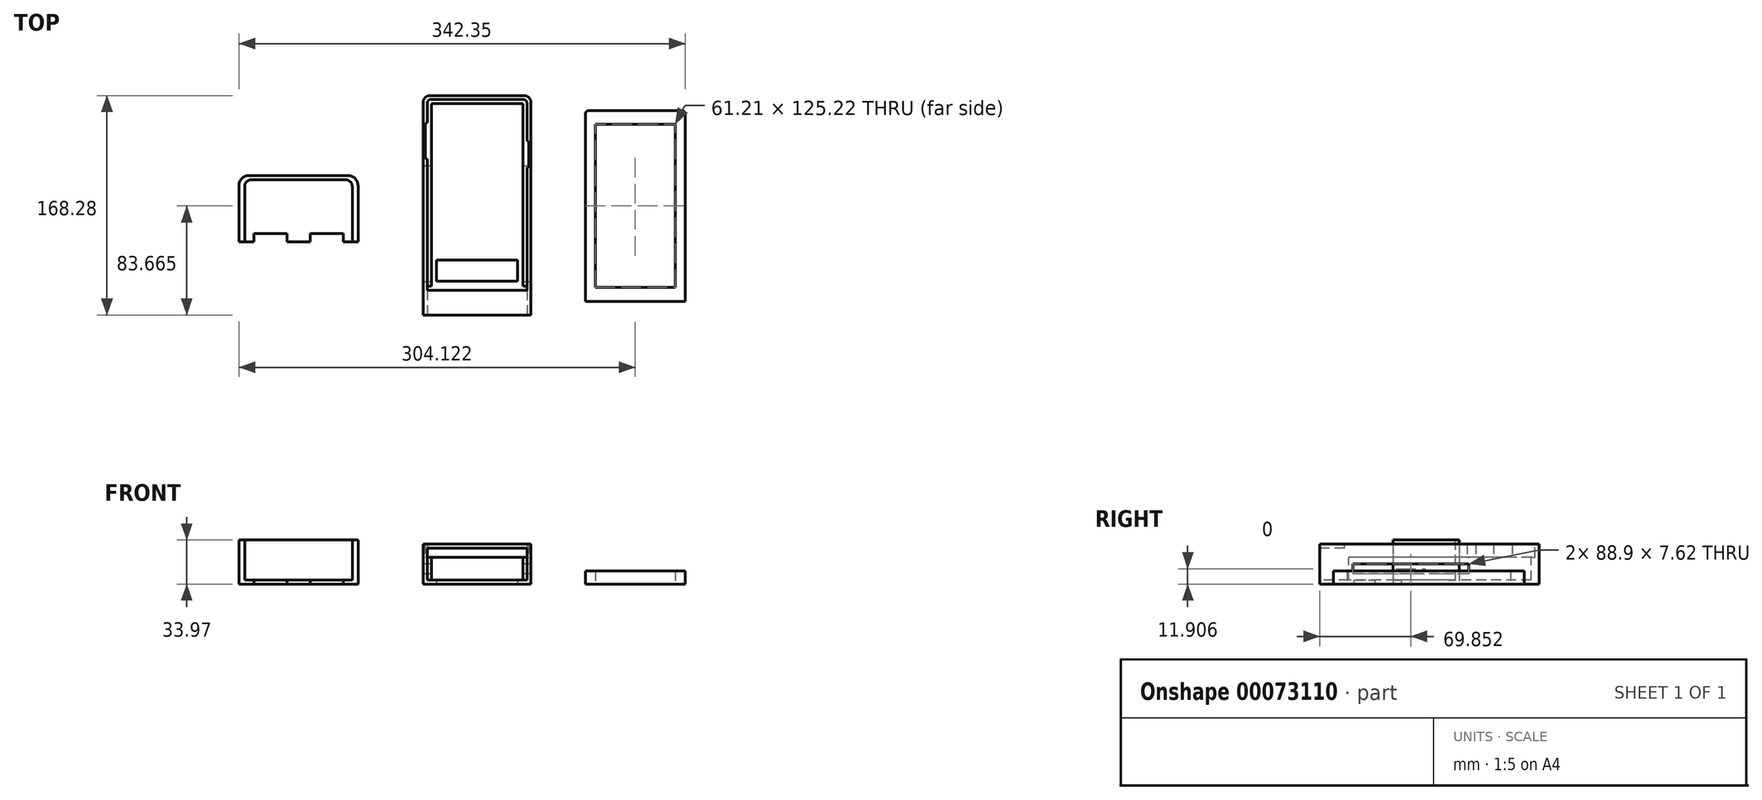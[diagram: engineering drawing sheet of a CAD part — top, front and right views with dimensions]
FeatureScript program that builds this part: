
annotation { "Feature Type Name" : "Feature", "Feature Type Description" : "" }
export const myFeature = defineFeature(function(context is Context, id is Id, definition is map)
    precondition{}
    {
        {
            var Q0;
            Q0=qCreatedBy(makeId("Top.planeOp"),FACE);
            var sketch = newSketch(context, id + "F0", { "sketchPlane" : qUnion([Q0])});
            skLineSegment(sketch, "E0.0", {"start": v(-45.8, 72.92) * mm, "end": v(36.75, 72.92) * mm});
            skLineSegment(sketch, "E0.1", {"start": v(-45.8, 72.92) * mm, "end": v(-45.8, -79.48) * mm});
            skLineSegment(sketch, "E0.2", {"start": v(-45.8, -79.48) * mm, "end": v(36.75, -79.48) * mm});
            skLineSegment(sketch, "E0.3", {"start": v(36.75, 72.92) * mm, "end": v(36.75, -79.48) * mm});
            skLineSegment(sketch, "E1", {"start": v(-45.8, -79.48) * mm, "end": v(-45.8, -95.36) * mm});
            skLineSegment(sketch, "E2", {"start": v(-45.8, -95.36) * mm, "end": v(36.75, -95.36) * mm});
            skLineSegment(sketch, "E3", {"start": v(36.75, -95.36) * mm, "end": v(36.75, -79.48) * mm});
            skLineSegment(sketch, "E4.bottom", {"start": v(-35.64, -69.32) * mm, "end": v(26.6, -69.32) * mm});
            skLineSegment(sketch, "E4.top", {"start": v(-35.64, -53.14) * mm, "end": v(26.6, -53.14) * mm});
            skLineSegment(sketch, "E4.left", {"start": v(-35.64, -69.32) * mm, "end": v(-35.64, -53.14) * mm});
            skLineSegment(sketch, "E4.right", {"start": v(26.6, -69.32) * mm, "end": v(26.6, -53.14) * mm});
            skSolve(sketch);
        }
        {
            var Q0;
            Q0=makeQuery(id+"F0.imprint","IMPRINT",FACE,{"disambiguationData":[TD([[makeQuery(id+"F0.imprint","IMPRINT",EDGE,{"derivedFrom":sQuery(id+"F0.wireOp",EDGE,"E0.0")}),-1.0]])]});
            extrude(context, id + "F1", {"entities" : qUnion([Q0]), "depth" : 30.8 * mm});
        }
        {
            var Q0;
            Q0=makeQuery(id+"F1.opExtrude","CAP_FACE",FACE,{"disambiguationData":[OSD([sQuery(id+"F0.wireOp",EDGE,"E0.0"),sQuery(id+"F0.wireOp",EDGE,"E0.1"),sQuery(id+"F0.wireOp",EDGE,"E0.2"),sQuery(id+"F0.wireOp",EDGE,"E0.3")])],"isStart":false});
            var sketch = newSketch(context, id + "F2", { "sketchPlane" : qUnion([Q0])});
            skLineSegment(sketch, "E5.0", {"start": v(-42.75, 69.87) * mm, "end": v(-42.75, -76.44) * mm});
            skLineSegment(sketch, "E5.1", {"start": v(-42.75, 69.87) * mm, "end": v(33.7, 69.87) * mm});
            skLineSegment(sketch, "E5.2", {"start": v(33.7, 69.87) * mm, "end": v(33.7, -76.44) * mm});
            skLineSegment(sketch, "E5.3", {"start": v(-42.75, -76.44) * mm, "end": v(33.7, -76.44) * mm});
            skSolve(sketch);
        }
        {
            var Q0;
            Q0=makeQuery(id+"F2.imprint","IMPRINT",FACE,{"disambiguationData":[TD([[makeQuery(id+"F2.imprint","IMPRINT",EDGE,{"derivedFrom":sQuery(id+"F2.wireOp",EDGE,"E5.0")}),1.0]])]});
            extrude(context, id + "F3", {"entities" : qUnion([Q0]), "operationType" : NewBodyOperationType.REMOVE, "oppositeDirection" : true, "depth" : 10.16 * mm});
        }
        {
            var Q0;
            Q0=makeQuery(id+"F3.boolean.opBoolean","COPY",FACE,{"derivedFrom":makeQuery(id+"F3.opExtrude","CAP_FACE",FACE,{"disambiguationData":[OSD([sQuery(id+"F2.wireOp",EDGE,"E5.0"),sQuery(id+"F2.wireOp",EDGE,"E5.1"),sQuery(id+"F2.wireOp",EDGE,"E5.2"),sQuery(id+"F2.wireOp",EDGE,"E5.3")])],"isStart":false})});
            var sketch = newSketch(context, id + "F4", { "sketchPlane" : qUnion([Q0])});
            skLineSegment(sketch, "E6.0", {"start": v(-39.57, 66.7) * mm, "end": v(30.53, 66.7) * mm});
            skLineSegment(sketch, "E6.1", {"start": v(-39.57, 66.7) * mm, "end": v(-39.57, -73.26) * mm});
            skLineSegment(sketch, "E6.2", {"start": v(-39.57, -73.26) * mm, "end": v(30.53, -73.26) * mm});
            skLineSegment(sketch, "E6.3", {"start": v(30.53, 66.7) * mm, "end": v(30.53, -73.26) * mm});
            skSolve(sketch);
        }
        {
            var Q0;
            Q0=makeQuery(id+"F4.imprint","IMPRINT",FACE,{"disambiguationData":[TD([[makeQuery(id+"F4.imprint","IMPRINT",EDGE,{"derivedFrom":sQuery(id+"F4.wireOp",EDGE,"E6.0")}),-1.0]])]});
            extrude(context, id + "F5", {"entities" : qUnion([Q0]), "operationType" : NewBodyOperationType.REMOVE, "oppositeDirection" : true, "depth" : 17.59 * mm});
        }
        {
            var Q0;
            Q0=makeQuery(id+"F0.imprint","IMPRINT",FACE,{"disambiguationData":[TD([[makeQuery(id+"F0.imprint","IMPRINT",EDGE,{"derivedFrom":sQuery(id+"F0.wireOp",EDGE,"E0.2")}),-1.0]])]});
            extrude(context, id + "F6", {"entities" : qUnion([Q0]), "operationType" : NewBodyOperationType.ADD, "depth" : 30.8 * mm});
        }
        {
            var Q0;
            Q0=makeQuery(id+"F6.opExtrude","SWEPT_FACE",FACE,{"disambiguationData":[OSD([sQuery(id+"F0.wireOp",EDGE,"E2")])]});
            var sketch = newSketch(context, id + "F7", { "sketchPlane" : qUnion([Q0])});
            skLineSegment(sketch, "E7.0", {"start": v(-42.75, 27.75) * mm, "end": v(33.7, 27.75) * mm});
            skLineSegment(sketch, "E7.1", {"start": v(-42.75, 27.75) * mm, "end": v(-42.75, 3.05) * mm});
            skLineSegment(sketch, "E7.2", {"start": v(-42.75, 3.05) * mm, "end": v(33.7, 3.05) * mm});
            skLineSegment(sketch, "E7.3", {"start": v(33.7, 27.75) * mm, "end": v(33.7, 3.05) * mm});
            skSolve(sketch);
        }
        {
            var Q0;
            Q0=makeQuery(id+"F7.imprint","IMPRINT",FACE,{"disambiguationData":[TD([[makeQuery(id+"F7.imprint","IMPRINT",EDGE,{"derivedFrom":sQuery(id+"F7.wireOp",EDGE,"E7.0")}),-1.0]])]});
            var Q1;
            Q1=makeQuery(id+"F5.boolean.opBoolean","COPY",FACE,{"derivedFrom":makeQuery(id+"F5.opExtrude","SWEPT_FACE",FACE,{"disambiguationData":[OSD([sQuery(id+"F4.wireOp",EDGE,"E6.2")])]})});
            extrude(context, id + "F8", {"entities" : qUnion([Q0]), "operationType" : NewBodyOperationType.REMOVE, "endBound" : BoundingType.UP_TO_SURFACE, "oppositeDirection" : true, "endBoundEntityFace" : qUnion([Q1]), "depth" : 20.48 * mm});
        }
        {
            var Q0;
            Q0=makeQuery(id+"F6.boolean.opBoolean","MERGE",FACE,{"derivedFrom":[makeQuery(id+"F1.opExtrude","SWEPT_FACE",FACE,{"disambiguationData":[OSD([sQuery(id+"F0.wireOp",EDGE,"E0.1")])]}),makeQuery(id+"F6.opExtrude","SWEPT_FACE",FACE,{"disambiguationData":[OSD([sQuery(id+"F0.wireOp",EDGE,"E1")])]})]});
            var sketch = newSketch(context, id + "F9", { "sketchPlane" : qUnion([Q0])});
            skLineSegment(sketch, "E8.bottom", {"start": v(-18.94, 15.72) * mm, "end": v(69.96, 15.72) * mm});
            skLineSegment(sketch, "E8.top", {"start": v(-18.94, 8.1) * mm, "end": v(69.96, 8.1) * mm});
            skLineSegment(sketch, "E8.left", {"start": v(-18.94, 15.72) * mm, "end": v(-18.94, 8.1) * mm});
            skLineSegment(sketch, "E8.right", {"start": v(69.96, 15.72) * mm, "end": v(69.96, 8.1) * mm});
            skSolve(sketch);
        }
        {
            var Q0;
            Q0=makeQuery(id+"F9.imprint","IMPRINT",FACE,{"disambiguationData":[TD([[makeQuery(id+"F9.imprint","IMPRINT",EDGE,{"derivedFrom":sQuery(id+"F9.wireOp",EDGE,"E8.bottom")}),-1.0]])]});
            var Q1;
            Q1=makeQuery(id+"F6.boolean.opBoolean","MERGE",FACE,{"derivedFrom":[makeQuery(id+"F1.opExtrude","SWEPT_FACE",FACE,{"disambiguationData":[OSD([sQuery(id+"F0.wireOp",EDGE,"E0.3")])]}),makeQuery(id+"F6.opExtrude","SWEPT_FACE",FACE,{"disambiguationData":[OSD([sQuery(id+"F0.wireOp",EDGE,"E3")])]})]});
            extrude(context, id + "F10", {"entities" : qUnion([Q0]), "operationType" : NewBodyOperationType.REMOVE, "endBound" : BoundingType.UP_TO_SURFACE, "oppositeDirection" : true, "endBoundEntityFace" : qUnion([Q1]), "depth" : 25.4 * mm});
        }
        {
            var Q0;
            Q0=makeQuery(id+"F1.opExtrude","SWEPT_EDGE",EDGE,{"disambiguationData":[OSD([sQuery(id+"F0.wireOp",EDGE,"E0.0"),sQuery(id+"F0.wireOp",EDGE,"E0.1")])]});
            var Q1;
            Q1=makeQuery(id+"F1.opExtrude","SWEPT_EDGE",EDGE,{"disambiguationData":[OSD([sQuery(id+"F0.wireOp",EDGE,"E0.0"),sQuery(id+"F0.wireOp",EDGE,"E0.3")])]});
            fillet(context, id + "F11", {"entities" : qUnion([Q0, Q1]), "radius" : 5.08 * mm, "tangentPropagation" : true, "allowEdgeOverflow" : false});
        }
        {
            var Q0;
            Q0=makeQuery(id+"F8.boolean.opBoolean","MERGE",FACE,{"derivedFrom":[makeQuery(id+"F3.boolean.opBoolean","COPY",FACE,{"derivedFrom":makeQuery(id+"F3.opExtrude","SWEPT_FACE",FACE,{"disambiguationData":[OSD([sQuery(id+"F2.wireOp",EDGE,"E5.0")])]})}),makeQuery(id+"F8.opExtrude","SWEPT_FACE",FACE,{"disambiguationData":[OSD([sQuery(id+"F7.wireOp",EDGE,"E7.1")])]})]});
            var sketch = newSketch(context, id + "F12", { "sketchPlane" : qUnion([Q0])});
            skLineSegment(sketch, "E9.bottom", {"start": v(52.09, 30.8) * mm, "end": v(24.15, 30.8) * mm});
            skLineSegment(sketch, "E9.top", {"start": v(52.09, 20.64) * mm, "end": v(24.15, 20.64) * mm});
            skLineSegment(sketch, "E9.left", {"start": v(52.09, 30.8) * mm, "end": v(52.09, 20.64) * mm});
            skLineSegment(sketch, "E9.right", {"start": v(24.15, 30.8) * mm, "end": v(24.15, 20.64) * mm});
            skSolve(sketch);
        }
        {
            var Q0;
            Q0=makeQuery(id+"F12.imprint","IMPRINT",FACE,{"disambiguationData":[TD([[makeQuery(id+"F12.imprint","IMPRINT",EDGE,{"derivedFrom":sQuery(id+"F12.wireOp",EDGE,"E9.bottom")}),1.0]])]});
            extrude(context, id + "F13", {"entities" : qUnion([Q0]), "operationType" : NewBodyOperationType.REMOVE, "oppositeDirection" : true, "depth" : 1.52 * mm});
        }
        {
            var Q0;
            Q0=makeQuery(id+"F13.boolean.opBoolean","COPY",EDGE,{"derivedFrom":makeQuery(id+"F13.opExtrude","CAP_EDGE",EDGE,{"disambiguationData":[OSD([sQuery(id+"F12.wireOp",EDGE,"E9.left")])],"isStart":false})});
            var Q1;
            Q1=makeQuery(id+"F13.boolean.opBoolean","COPY",EDGE,{"derivedFrom":makeQuery(id+"F13.opExtrude","CAP_EDGE",EDGE,{"disambiguationData":[OSD([sQuery(id+"F12.wireOp",EDGE,"E9.right")])],"isStart":false})});
            fillet(context, id + "F14", {"entities" : qUnion([Q0, Q1]), "radius" : 1.52 * mm, "tangentPropagation" : true, "allowEdgeOverflow" : false});
        }
        {
            var Q0;
            Q0=makeQuery(id+"F8.boolean.opBoolean","MERGE",FACE,{"derivedFrom":[makeQuery(id+"F3.boolean.opBoolean","COPY",FACE,{"derivedFrom":makeQuery(id+"F3.opExtrude","SWEPT_FACE",FACE,{"disambiguationData":[OSD([sQuery(id+"F2.wireOp",EDGE,"E5.2")])]})}),makeQuery(id+"F8.opExtrude","SWEPT_FACE",FACE,{"disambiguationData":[OSD([sQuery(id+"F7.wireOp",EDGE,"E7.3")])]})]});
            var sketch = newSketch(context, id + "F15", { "sketchPlane" : qUnion([Q0])});
            skLineSegment(sketch, "E10.bottom", {"start": v(-38.12, 30.8) * mm, "end": v(-17.8, 30.8) * mm});
            skLineSegment(sketch, "E10.top", {"start": v(-38.12, 20.64) * mm, "end": v(-17.8, 20.64) * mm});
            skLineSegment(sketch, "E10.left", {"start": v(-38.12, 30.8) * mm, "end": v(-38.12, 20.64) * mm});
            skLineSegment(sketch, "E10.right", {"start": v(-17.8, 30.8) * mm, "end": v(-17.8, 20.64) * mm});
            skSolve(sketch);
        }
        {
            var Q0;
            Q0=makeQuery(id+"F15.imprint","IMPRINT",FACE,{"disambiguationData":[TD([[makeQuery(id+"F15.imprint","IMPRINT",EDGE,{"derivedFrom":sQuery(id+"F15.wireOp",EDGE,"E10.bottom")}),-1.0]])]});
            extrude(context, id + "F16", {"entities" : qUnion([Q0]), "operationType" : NewBodyOperationType.REMOVE, "oppositeDirection" : true, "depth" : 1.52 * mm});
        }
        {
            var Q0;
            Q0=makeQuery(id+"F16.boolean.opBoolean","COPY",EDGE,{"derivedFrom":makeQuery(id+"F16.opExtrude","CAP_EDGE",EDGE,{"disambiguationData":[OSD([sQuery(id+"F15.wireOp",EDGE,"E10.left")])],"isStart":false})});
            var Q1;
            Q1=makeQuery(id+"F16.boolean.opBoolean","COPY",EDGE,{"derivedFrom":makeQuery(id+"F16.opExtrude","CAP_EDGE",EDGE,{"disambiguationData":[OSD([sQuery(id+"F15.wireOp",EDGE,"E10.right")])],"isStart":false})});
            fillet(context, id + "F17", {"entities" : qUnion([Q0, Q1]), "radius" : 1.52 * mm, "tangentPropagation" : true, "allowEdgeOverflow" : false});
        }
        {
            var Q0;
            Q0=makeQuery(id+"F3.boolean.opBoolean","COPY",EDGE,{"derivedFrom":makeQuery(id+"F3.opExtrude","SWEPT_EDGE",EDGE,{"disambiguationData":[OSD([sQuery(id+"F2.wireOp",EDGE,"E5.0"),sQuery(id+"F2.wireOp",EDGE,"E5.1")])]})});
            var Q1;
            Q1=makeQuery(id+"F3.boolean.opBoolean","COPY",EDGE,{"derivedFrom":makeQuery(id+"F3.opExtrude","SWEPT_EDGE",EDGE,{"disambiguationData":[OSD([sQuery(id+"F2.wireOp",EDGE,"E5.1"),sQuery(id+"F2.wireOp",EDGE,"E5.2")])]})});
            fillet(context, id + "F18", {"entities" : qUnion([Q0, Q1]), "radius" : 2.54 * mm, "tangentPropagation" : true, "allowEdgeOverflow" : false});
        }
        {
            var Q0;
            Q0=qCreatedBy(makeId("Top.planeOp"),FACE);
            var sketch = newSketch(context, id + "F19", { "sketchPlane" : qUnion([Q0])});
            skLineSegment(sketch, "E11.bottom", {"start": v(-187.26, 11.56) * mm, "end": v(-95.82, 11.56) * mm});
            skLineSegment(sketch, "E11.top", {"start": v(-187.26, -39.24) * mm, "end": v(-95.82, -39.24) * mm});
            skLineSegment(sketch, "E11.left", {"start": v(-187.26, 11.56) * mm, "end": v(-187.26, -39.24) * mm});
            skLineSegment(sketch, "E11.right", {"start": v(-95.82, 11.56) * mm, "end": v(-95.82, -39.24) * mm});
            skLineSegment(sketch, "E12.bottom", {"start": v(-175.83, -39.24) * mm, "end": v(-150.43, -39.24) * mm});
            skLineSegment(sketch, "E12.top", {"start": v(-175.83, -32.89) * mm, "end": v(-150.43, -32.89) * mm});
            skLineSegment(sketch, "E12.left", {"start": v(-175.83, -39.24) * mm, "end": v(-175.83, -32.89) * mm});
            skLineSegment(sketch, "E12.right", {"start": v(-150.43, -39.24) * mm, "end": v(-150.43, -32.89) * mm});
            skLineSegment(sketch, "E13.bottom", {"start": v(-132.65, -39.24) * mm, "end": v(-107.25, -39.24) * mm});
            skLineSegment(sketch, "E13.top", {"start": v(-132.65, -32.89) * mm, "end": v(-107.25, -32.89) * mm});
            skLineSegment(sketch, "E13.left", {"start": v(-132.65, -39.24) * mm, "end": v(-132.65, -32.89) * mm});
            skLineSegment(sketch, "E13.right", {"start": v(-107.25, -39.24) * mm, "end": v(-107.25, -32.89) * mm});
            skSolve(sketch);
        }
        {
            var Q0;
            Q0=makeQuery(id+"F19.imprint","IMPRINT",FACE,{"disambiguationData":[TD([[makeQuery(id+"F19.imprint","IMPRINT",EDGE,{"derivedFrom":sQuery(id+"F19.wireOp",EDGE,"E11.bottom")}),-1.0]])]});
            extrude(context, id + "F20", {"entities" : qUnion([Q0]), "depth" : 3.17 * mm});
        }
        {
            var Q0;
            Q0=makeQuery(id+"F20.opExtrude","SWEPT_EDGE",EDGE,{"disambiguationData":[OSD([sQuery(id+"F19.wireOp",EDGE,"E11.bottom"),sQuery(id+"F19.wireOp",EDGE,"E11.left")])]});
            var Q1;
            Q1=makeQuery(id+"F20.opExtrude","SWEPT_EDGE",EDGE,{"disambiguationData":[OSD([sQuery(id+"F19.wireOp",EDGE,"E11.bottom"),sQuery(id+"F19.wireOp",EDGE,"E11.right")])]});
            fillet(context, id + "F21", {"entities" : qUnion([Q0, Q1]), "radius" : 7.62 * mm, "tangentPropagation" : true, "allowEdgeOverflow" : false});
        }
        {
            var Q0;
            Q0=makeQuery(id+"F20.opExtrude","CAP_FACE",FACE,{"disambiguationData":[OSD([sQuery(id+"F19.wireOp",EDGE,"E11.bottom"),sQuery(id+"F19.wireOp",EDGE,"E11.top"),sQuery(id+"F19.wireOp",EDGE,"E11.left"),sQuery(id+"F19.wireOp",EDGE,"E11.right")])],"isStart":false});
            var sketch = newSketch(context, id + "F22", { "sketchPlane" : qUnion([Q0])});
            skLineSegment(sketch, "E14.bottom", {"start": v(-182.82, 8.39) * mm, "end": v(-100.27, 8.39) * mm});
            skLineSegment(sketch, "E14.top", {"start": v(-182.82, -39.24) * mm, "end": v(-100.27, -39.24) * mm});
            skLineSegment(sketch, "E14.left", {"start": v(-182.82, 8.39) * mm, "end": v(-182.82, -39.24) * mm});
            skLineSegment(sketch, "E14.right", {"start": v(-100.27, 8.39) * mm, "end": v(-100.27, -39.24) * mm});
            skSolve(sketch);
        }
        {
            var Q0;
            Q0=makeQuery(id+"F22.imprint","IMPRINT",FACE,{"disambiguationData":[TD([[makeQuery(id+"F22.imprint","IMPRINT",EDGE,{"derivedFrom":sQuery(id+"F22.wireOp",EDGE,"E14.bottom")}),1.0]])]});
            extrude(context, id + "F23", {"entities" : qUnion([Q0]), "operationType" : NewBodyOperationType.ADD, "depth" : 30.8 * mm});
        }
        {
            var Q0;
            Q0=makeQuery(id+"F23.opExtrude","SWEPT_EDGE",EDGE,{"disambiguationData":[OSD([sQuery(id+"F22.wireOp",EDGE,"E14.bottom"),sQuery(id+"F22.wireOp",EDGE,"E14.left")])]});
            var Q1;
            Q1=makeQuery(id+"F23.opExtrude","SWEPT_EDGE",EDGE,{"disambiguationData":[OSD([sQuery(id+"F22.wireOp",EDGE,"E14.bottom"),sQuery(id+"F22.wireOp",EDGE,"E14.right")])]});
            fillet(context, id + "F24", {"entities" : qUnion([Q0, Q1]), "radius" : 5.08 * mm, "tangentPropagation" : true, "allowEdgeOverflow" : false});
        }
        {
            var Q0;
            Q0=qCreatedBy(makeId("Top.planeOp"),FACE);
            var sketch = newSketch(context, id + "F25", { "sketchPlane" : qUnion([Q0])});
            skLineSegment(sketch, "E15.bottom", {"start": v(78.64, 61.46) * mm, "end": v(155.09, 61.46) * mm});
            skLineSegment(sketch, "E15.top", {"start": v(78.64, -84.85) * mm, "end": v(155.09, -84.85) * mm});
            skLineSegment(sketch, "E15.left", {"start": v(78.64, 61.46) * mm, "end": v(78.64, -84.85) * mm});
            skLineSegment(sketch, "E15.right", {"start": v(155.09, 61.46) * mm, "end": v(155.09, -84.85) * mm});
            skLineSegment(sketch, "E16.bottom", {"start": v(86.26, 50.92) * mm, "end": v(147.47, 50.92) * mm});
            skLineSegment(sketch, "E16.top", {"start": v(86.26, -74.3) * mm, "end": v(147.47, -74.3) * mm});
            skLineSegment(sketch, "E16.left", {"start": v(86.26, 50.92) * mm, "end": v(86.26, -74.3) * mm});
            skLineSegment(sketch, "E16.right", {"start": v(147.47, 50.92) * mm, "end": v(147.47, -74.3) * mm});
            skSolve(sketch);
        }
        {
            var Q0;
            Q0=makeQuery(id+"F25.imprint","IMPRINT",FACE,{"disambiguationData":[TD([[makeQuery(id+"F25.imprint","IMPRINT",EDGE,{"derivedFrom":sQuery(id+"F25.wireOp",EDGE,"E15.bottom")}),-1.0]])]});
            extrude(context, id + "F26", {"entities" : qUnion([Q0]), "depth" : 10.16 * mm});
        }
        {
            var Q0;
            Q0=makeQuery(id+"F26.opExtrude","SWEPT_EDGE",EDGE,{"disambiguationData":[OSD([sQuery(id+"F25.wireOp",EDGE,"E15.bottom"),sQuery(id+"F25.wireOp",EDGE,"E15.left")])]});
            var Q1;
            Q1=makeQuery(id+"F26.opExtrude","SWEPT_EDGE",EDGE,{"disambiguationData":[OSD([sQuery(id+"F25.wireOp",EDGE,"E15.bottom"),sQuery(id+"F25.wireOp",EDGE,"E15.right")])]});
            fillet(context, id + "F27", {"entities" : qUnion([Q0, Q1]), "radius" : 2.54 * mm, "tangentPropagation" : true, "allowEdgeOverflow" : false});
        }
    });
